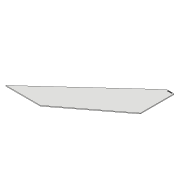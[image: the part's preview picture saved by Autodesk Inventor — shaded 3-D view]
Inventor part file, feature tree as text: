
AUTODESK INVENTOR PART (.ipt)
format: ipt  version: 2018 (Build 220112000, 112)  size: 138,752 bytes
history: native  units: in
note: dims shown in document units (in); Inventor stores cm internally (conversion verified against a paired STEP export)
features: other x5, extrude x3, sketch x3, fillet x1, projected_geometry x1
ambient origin geometry x8: Origin, YZ Plane, XZ Plane, XY Plane, X Axis, Y Axis, Z Axis, Center Point
bodies: Solid1 (feature_tree), Solid2 (feature_tree)
feature tree (13):
  other  "Table"
  other  "OuterHCALtile9"
  other  "OuterHCALtile10"
  other  "OuterHCALtile11"
  other  "OuterHCALtile12"
  extrude  "Extrusion1"  Depth=27.4567in
  extrude  "Extrusion2"  Depth=0.2756in
  fillet  "Fillet1"  Radius=0.2756in
  extrude  "Extrusion3"  TaperAngle=75.0deg  [1 undecoded]
  sketch  "Sketch1"  dims[d0=12.311in d2=27.4567in]
  sketch  "Sketch2"  dims[d4=0.3618in d5=0.3266in d6=0.2756in d7=0.0in]
  projected_geometry  "Projected Loop1"
  sketch  "Sketch3"  dims[d8=11.9882in d9=75.0deg d10=75.0deg d11=0.3563in d12=0.4319in d13=31.7047in d14=1.6122in d15=0.2756in d16=0.0in d17=0.0394in d18=0.0394in d19=0.2756in d20=0.0in]
note: 1 required parameter value undecoded (feature->parameter linkage not recoverable at this tier; creation-order binding heuristic only, values carry confidence <= 0.55)
